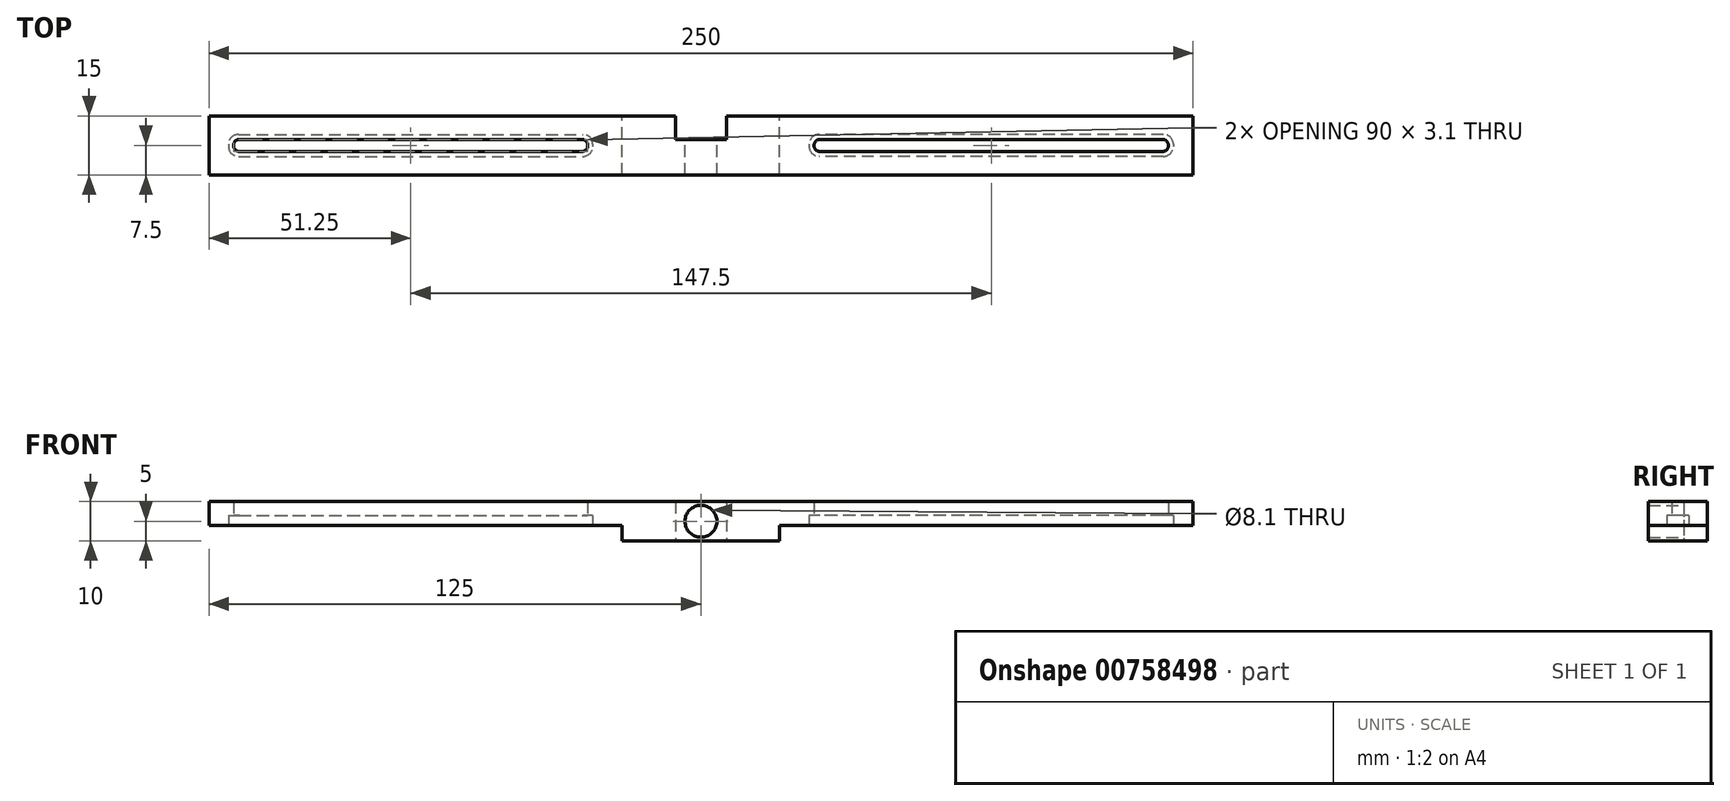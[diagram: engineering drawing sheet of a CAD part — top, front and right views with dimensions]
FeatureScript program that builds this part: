
annotation { "Feature Type Name" : "Feature", "Feature Type Description" : "" }
export const myFeature = defineFeature(function(context is Context, id is Id, definition is map)
    precondition{}
    {
        {
            var Q0;
            Q0=qCreatedBy(makeId("Top.planeOp"),FACE);
            var sketch = newSketch(context, id + "F0", { "sketchPlane" : qUnion([Q0])});
            skLineSegment(sketch, "E0.bottom", {"start": v(125, 7.5) * mm, "end": v(-125, 7.5) * mm});
            skLineSegment(sketch, "E0.top", {"start": v(125, -7.5) * mm, "end": v(-125, -7.5) * mm});
            skLineSegment(sketch, "E0.left", {"start": v(125, 7.5) * mm, "end": v(125, -7.5) * mm});
            skLineSegment(sketch, "E0.right", {"start": v(-125, 7.5) * mm, "end": v(-125, -7.5) * mm});
            skPoint(sketch, "E0.middle", {"position": v(0, 0) * mm});
            skLineSegment(sketch, "E1.bottom", {"start": v(-118.75, 1.55) * mm, "end": v(-28.75, 1.55) * mm});
            skLineSegment(sketch, "E1.top", {"start": v(-118.75, -1.55) * mm, "end": v(-28.75, -1.55) * mm});
            skLineSegment(sketch, "E1.left", {"start": v(-118.75, 1.55) * mm, "end": v(-118.75, -1.55) * mm});
            skLineSegment(sketch, "E1.right", {"start": v(-28.75, 1.55) * mm, "end": v(-28.75, -1.55) * mm});
            skPoint(sketch, "E1.middle", {"position": v(-73.75, 0) * mm});
            skLineSegment(sketch, "E2.0", {"start": v(-120, 2.8) * mm, "end": v(-27.5, 2.8) * mm});
            skLineSegment(sketch, "E2.1", {"start": v(-120, 2.8) * mm, "end": v(-120, -2.8) * mm});
            skLineSegment(sketch, "E2.2", {"start": v(-120, -2.8) * mm, "end": v(-27.5, -2.8) * mm});
            skLineSegment(sketch, "E2.3", {"start": v(-27.5, 2.8) * mm, "end": v(-27.5, -2.8) * mm});
            skLineSegment(sketch, "E3.MirrorCS", {"start": v(118.75, 1.55) * mm, "end": v(28.75, 1.55) * mm});
            skLineSegment(sketch, "E4.MirrorCS", {"start": v(120, 2.8) * mm, "end": v(27.5, 2.8) * mm});
            skLineSegment(sketch, "E5.MirrorCS", {"start": v(28.75, 1.55) * mm, "end": v(28.75, -1.55) * mm});
            skLineSegment(sketch, "E6.MirrorCS", {"start": v(118.75, 1.55) * mm, "end": v(118.75, -1.55) * mm});
            skLineSegment(sketch, "E7.MirrorCS", {"start": v(118.75, -1.55) * mm, "end": v(28.75, -1.55) * mm});
            skPoint(sketch, "E8.MirrorP", {"position": v(73.75, 0) * mm});
            skLineSegment(sketch, "E9.MirrorCS", {"start": v(27.5, 2.8) * mm, "end": v(27.5, -2.8) * mm});
            skLineSegment(sketch, "E10.MirrorCS", {"start": v(120, 2.8) * mm, "end": v(120, -2.8) * mm});
            skLineSegment(sketch, "E11.MirrorCS", {"start": v(120, -2.8) * mm, "end": v(27.5, -2.8) * mm});
            skLineSegment(sketch, "E12.bottom", {"start": v(-20, -7.5) * mm, "end": v(20, -7.5) * mm});
            skLineSegment(sketch, "E12.top", {"start": v(-20, 7.5) * mm, "end": v(20, 7.5) * mm});
            skLineSegment(sketch, "E12.left", {"start": v(-20, -7.5) * mm, "end": v(-20, 7.5) * mm});
            skLineSegment(sketch, "E12.right", {"start": v(20, -7.5) * mm, "end": v(20, 7.5) * mm});
            skSolve(sketch);
        }
        {
            var Q0;
            {var subQ0=sQuery(id+"F0.wireOp",EDGE,"E0.right");var subQ4=sQuery(id+"F0.wireOp",EDGE,"E0.left");Q0=qUnion([makeQuery(id+"F0.imprint","IMPRINT",FACE,{"disambiguationData":[TD([[makeQuery(id+"F0.imprint","IMPRINT",EDGE,{"derivedFrom":subQ4}),-1.0]])]}),makeQuery(id+"F0.imprint","IMPRINT",FACE,{"disambiguationData":[TD([[makeQuery(id+"F0.imprint","IMPRINT",EDGE,{"derivedFrom":subQ0}),1.0]])]})]);}
            var Q1;
            Q1=makeQuery(id+"F0.imprint","IMPRINT",FACE,{"disambiguationData":[TD([[makeQuery(id+"F0.imprint","IMPRINT",EDGE,{"derivedFrom":sQuery(id+"F0.wireOp",EDGE,"E1.bottom")}),1.0]])]});
            var Q2;
            Q2=makeQuery(id+"F0.imprint","IMPRINT",FACE,{"disambiguationData":[TD([[makeQuery(id+"F0.imprint","IMPRINT",EDGE,{"derivedFrom":sQuery(id+"F0.wireOp",EDGE,"E3.MirrorCS")}),-1.0]])]});
            var Q3;
            {var subQ0=sQuery(id+"F0.wireOp",EDGE,"E12.left");Q3=makeQuery(id+"F0.imprint","IMPRINT",FACE,{"disambiguationData":[TD([[makeQuery(id+"F0.imprint","IMPRINT",EDGE,{"derivedFrom":subQ0}),-1.0]])]});}
            extrude(context, id + "F1", {"entities" : qUnion([Q0, Q1, Q2, Q3]), "depth" : 10 * mm, "offsetDistance" : 25 * mm});
        }
        {
            var Q0;
            Q0=makeQuery(id+"F0.imprint","IMPRINT",FACE,{"disambiguationData":[TD([[makeQuery(id+"F0.imprint","IMPRINT",EDGE,{"derivedFrom":sQuery(id+"F0.wireOp",EDGE,"E3.MirrorCS")}),-1.0]])]});
            var Q1;
            Q1=makeQuery(id+"F0.imprint","IMPRINT",FACE,{"disambiguationData":[TD([[makeQuery(id+"F0.imprint","IMPRINT",EDGE,{"derivedFrom":sQuery(id+"F0.wireOp",EDGE,"E1.bottom")}),1.0]])]});
            extrude(context, id + "F2", {"entities" : qUnion([Q0, Q1]), "operationType" : NewBodyOperationType.REMOVE, "depth" : 6.5 * mm, "offsetDistance" : 25 * mm});
        }
        {
            var Q0;
            Q0=makeQuery(id+"F1.opExtrude","SWEPT_FACE",FACE,{"disambiguationData":[OSD([sQuery(id+"F0.wireOp",EDGE,"E0.bottom")])]});
            var sketch = newSketch(context, id + "F3", { "sketchPlane" : qUnion([Q0])});
            skLineSegment(sketch, "E13.bottom", {"start": v(6.5, 14.5) * mm, "end": v(-6.5, 14.5) * mm});
            skLineSegment(sketch, "E13.top", {"start": v(6.5, -4.5) * mm, "end": v(-6.5, -4.5) * mm});
            skLineSegment(sketch, "E13.left", {"start": v(6.5, 14.5) * mm, "end": v(6.5, -4.5) * mm});
            skLineSegment(sketch, "E13.right", {"start": v(-6.5, 14.5) * mm, "end": v(-6.5, -4.5) * mm});
            skPoint(sketch, "E13.middle", {"position": v(0, 5) * mm});
            skSolve(sketch);
        }
        {
            var Q0;
            {var subQ0=sQuery(id+"F3.wireOp",EDGE,"E13.left");var subQ1=sQuery(id+"F0.wireOp",EDGE,"E0.bottom");var subQ2=makeQuery(id+"F1.opExtrude","CAP_EDGE",EDGE,{"disambiguationData":[OSD([subQ1])],"isStart":false});var subQ3=makeQuery(id+"F3.imprint","INTERSECT",VERTEX,{"derivedFrom":[subQ2,subQ0]});Q0=makeQuery(id+"F3.imprint","IMPRINT",FACE,{"disambiguationData":[TD([[makeQuery(id+"F3.imprint","IMPRINT",EDGE,{"disambiguationData":[TD([[subQ3,-1.0]])],"derivedFrom":subQ0}),-1.0]])]});}
            extrude(context, id + "F4", {"entities" : qUnion([Q0]), "operationType" : NewBodyOperationType.REMOVE, "oppositeDirection" : true, "depth" : 6 * mm, "offsetDistance" : 25 * mm});
        }
        {
            var Q0;
            Q0=sQuery(id+"F3.wireOp",VERTEX,"E13.middle");
            var Q1;
            Q1=makeQuery(id+"F1.opExtrude","SWEPT_BODY",BODY,{"disambiguationData":[OSD([sQuery(id+"F0.wireOp",EDGE,"E0.bottom"),sQuery(id+"F0.wireOp",EDGE,"E0.top"),sQuery(id+"F0.wireOp",EDGE,"E0.left"),sQuery(id+"F0.wireOp",EDGE,"E0.right"),sQuery(id+"F0.wireOp",EDGE,"E1.bottom"),sQuery(id+"F0.wireOp",EDGE,"E1.top"),sQuery(id+"F0.wireOp",EDGE,"E1.left"),sQuery(id+"F0.wireOp",EDGE,"E1.right"),sQuery(id+"F0.wireOp",EDGE,"E3.MirrorCS"),sQuery(id+"F0.wireOp",EDGE,"E5.MirrorCS"),sQuery(id+"F0.wireOp",EDGE,"E6.MirrorCS"),sQuery(id+"F0.wireOp",EDGE,"E7.MirrorCS")])]});
            hole(context, id + "F5", {"style" : HoleStyle.SIMPLE, "endStyle" : HoleEndStyle.BLIND, "holeDiameter" : 8.1 * mm, "majorDiameter" : 5 * mm, "holeDepth" : 22 * mm, "isTappedThrough" : true, "tappedDepth" : 12 * mm, "tapClearance" : 3, "locations" : qUnion([Q0]), "scope" : qUnion([Q1])});
        }
        {
            var Q0;
            {var subQ0=sQuery(id+"F0.wireOp",EDGE,"E0.right");Q0=makeQuery(id+"F0.imprint","IMPRINT",FACE,{"disambiguationData":[TD([[makeQuery(id+"F0.imprint","IMPRINT",EDGE,{"derivedFrom":subQ0}),1.0]])]});}
            var Q1;
            {var subQ0=sQuery(id+"F0.wireOp",EDGE,"E0.left");Q1=makeQuery(id+"F0.imprint","IMPRINT",FACE,{"disambiguationData":[TD([[makeQuery(id+"F0.imprint","IMPRINT",EDGE,{"derivedFrom":subQ0}),-1.0]])]});}
            extrude(context, id + "F6", {"entities" : qUnion([Q0, Q1]), "operationType" : NewBodyOperationType.REMOVE, "depth" : 4 * mm, "offsetDistance" : 25 * mm});
        }
        {
            var Q0;
            Q0=makeQuery(id+"F2.boolean.opBoolean","COPY",EDGE,{"derivedFrom":makeQuery(id+"F2.opExtrude","SWEPT_EDGE",EDGE,{"disambiguationData":[OSD([sQuery(id+"F0.wireOp",EDGE,"E2.0"),sQuery(id+"F0.wireOp",EDGE,"E2.3")])]})});
            var Q1;
            Q1=makeQuery(id+"F2.boolean.opBoolean","COPY",EDGE,{"derivedFrom":makeQuery(id+"F2.opExtrude","SWEPT_EDGE",EDGE,{"disambiguationData":[OSD([sQuery(id+"F0.wireOp",EDGE,"E2.2"),sQuery(id+"F0.wireOp",EDGE,"E2.3")])]})});
            var Q2;
            Q2=makeQuery(id+"F2.boolean.opBoolean","COPY",EDGE,{"derivedFrom":makeQuery(id+"F2.opExtrude","SWEPT_EDGE",EDGE,{"disambiguationData":[OSD([sQuery(id+"F0.wireOp",EDGE,"E2.0"),sQuery(id+"F0.wireOp",EDGE,"E2.1")])]})});
            var Q3;
            Q3=makeQuery(id+"F2.boolean.opBoolean","COPY",EDGE,{"derivedFrom":makeQuery(id+"F2.opExtrude","SWEPT_EDGE",EDGE,{"disambiguationData":[OSD([sQuery(id+"F0.wireOp",EDGE,"E2.1"),sQuery(id+"F0.wireOp",EDGE,"E2.2")])]})});
            var Q4;
            Q4=makeQuery(id+"F2.boolean.opBoolean","COPY",EDGE,{"derivedFrom":makeQuery(id+"F2.opExtrude","SWEPT_EDGE",EDGE,{"disambiguationData":[OSD([sQuery(id+"F0.wireOp",EDGE,"E9.MirrorCS"),sQuery(id+"F0.wireOp",EDGE,"E11.MirrorCS")])]})});
            var Q5;
            Q5=makeQuery(id+"F2.boolean.opBoolean","COPY",EDGE,{"derivedFrom":makeQuery(id+"F2.opExtrude","SWEPT_EDGE",EDGE,{"disambiguationData":[OSD([sQuery(id+"F0.wireOp",EDGE,"E10.MirrorCS"),sQuery(id+"F0.wireOp",EDGE,"E11.MirrorCS")])]})});
            var Q6;
            Q6=makeQuery(id+"F2.boolean.opBoolean","COPY",EDGE,{"derivedFrom":makeQuery(id+"F2.opExtrude","SWEPT_EDGE",EDGE,{"disambiguationData":[OSD([sQuery(id+"F0.wireOp",EDGE,"E4.MirrorCS"),sQuery(id+"F0.wireOp",EDGE,"E10.MirrorCS")])]})});
            var Q7;
            Q7=makeQuery(id+"F2.boolean.opBoolean","COPY",EDGE,{"derivedFrom":makeQuery(id+"F2.opExtrude","SWEPT_EDGE",EDGE,{"disambiguationData":[OSD([sQuery(id+"F0.wireOp",EDGE,"E4.MirrorCS"),sQuery(id+"F0.wireOp",EDGE,"E9.MirrorCS")])]})});
            fillet(context, id + "F7", {"entities" : qUnion([Q0, Q1, Q2, Q3, Q4, Q5, Q6, Q7]), "radius" : 2.5 * mm, "tangentPropagation" : true, "allowEdgeOverflow" : false});
        }
        {
            var Q0;
            Q0=makeQuery(id+"F1.opExtrude","SWEPT_EDGE",EDGE,{"disambiguationData":[OSD([sQuery(id+"F0.wireOp",EDGE,"E3.MirrorCS"),sQuery(id+"F0.wireOp",EDGE,"E5.MirrorCS")])]});
            var Q1;
            Q1=makeQuery(id+"F1.opExtrude","SWEPT_EDGE",EDGE,{"disambiguationData":[OSD([sQuery(id+"F0.wireOp",EDGE,"E5.MirrorCS"),sQuery(id+"F0.wireOp",EDGE,"E7.MirrorCS")])]});
            var Q2;
            Q2=makeQuery(id+"F1.opExtrude","SWEPT_EDGE",EDGE,{"disambiguationData":[OSD([sQuery(id+"F0.wireOp",EDGE,"E3.MirrorCS"),sQuery(id+"F0.wireOp",EDGE,"E6.MirrorCS")])]});
            var Q3;
            Q3=makeQuery(id+"F1.opExtrude","SWEPT_EDGE",EDGE,{"disambiguationData":[OSD([sQuery(id+"F0.wireOp",EDGE,"E6.MirrorCS"),sQuery(id+"F0.wireOp",EDGE,"E7.MirrorCS")])]});
            var Q4;
            Q4=makeQuery(id+"F1.opExtrude","SWEPT_EDGE",EDGE,{"disambiguationData":[OSD([sQuery(id+"F0.wireOp",EDGE,"E1.top"),sQuery(id+"F0.wireOp",EDGE,"E1.right")])]});
            var Q5;
            Q5=makeQuery(id+"F1.opExtrude","SWEPT_EDGE",EDGE,{"disambiguationData":[OSD([sQuery(id+"F0.wireOp",EDGE,"E1.bottom"),sQuery(id+"F0.wireOp",EDGE,"E1.right")])]});
            var Q6;
            Q6=makeQuery(id+"F1.opExtrude","SWEPT_EDGE",EDGE,{"disambiguationData":[OSD([sQuery(id+"F0.wireOp",EDGE,"E1.bottom"),sQuery(id+"F0.wireOp",EDGE,"E1.left")])]});
            var Q7;
            Q7=makeQuery(id+"F1.opExtrude","SWEPT_EDGE",EDGE,{"disambiguationData":[OSD([sQuery(id+"F0.wireOp",EDGE,"E1.top"),sQuery(id+"F0.wireOp",EDGE,"E1.left")])]});
            fillet(context, id + "F8", {"entities" : qUnion([Q0, Q1, Q2, Q3, Q4, Q5, Q6, Q7]), "radius" : 1.5 * mm, "tangentPropagation" : true, "allowEdgeOverflow" : false});
        }
    });
